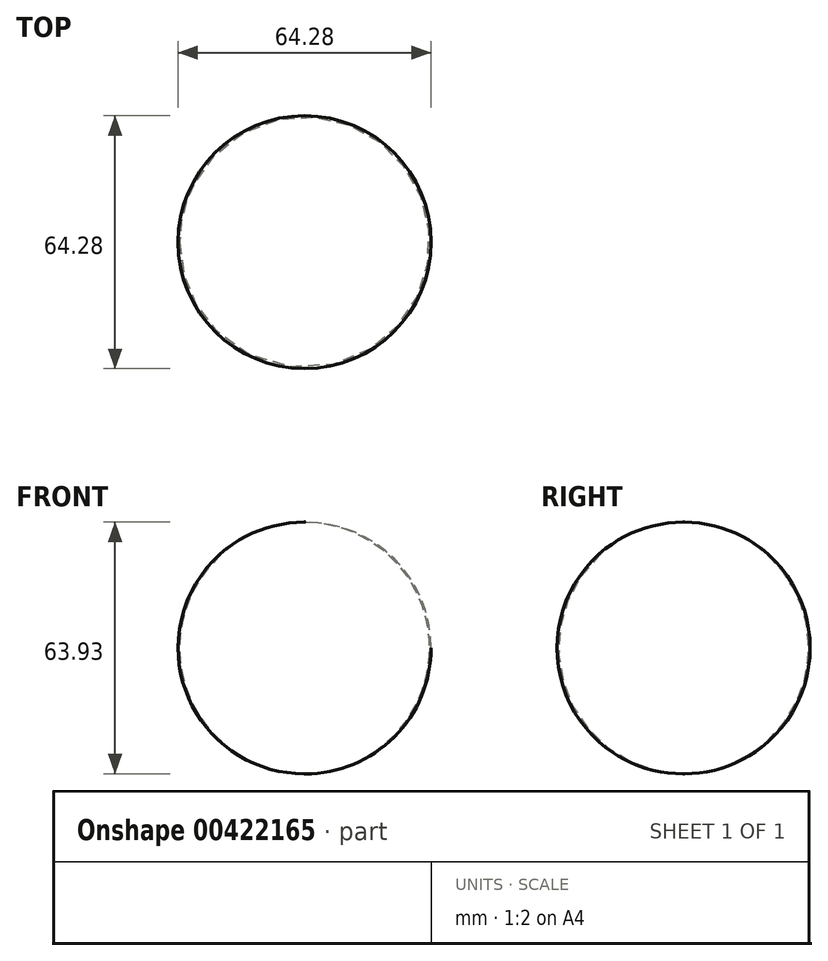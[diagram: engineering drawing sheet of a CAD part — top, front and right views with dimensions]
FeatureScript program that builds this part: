
annotation { "Feature Type Name" : "Feature", "Feature Type Description" : "" }
export const myFeature = defineFeature(function(context is Context, id is Id, definition is map)
    precondition{}
    {
        {
            var Q0;
            Q0=qCreatedBy(makeId("Front.planeOp"),FACE);
            var sketch = newSketch(context, id + "F0", { "sketchPlane" : qUnion([Q0])});
            skArc(sketch, "E0", {"start": v(0, -24.37) * mm, "mid": v(31.79, 7.6) * mm, "end": v(0, 39.56) * mm});
            skLineSegment(sketch, "E1", {"start": v(0, 39.56) * mm, "end": v(0, -24.37) * mm});
            skSolve(sketch);
        }
        {
            var Q0;
            Q0 = qSketchRegion(id + "F0", true);
            var Q1;
            Q1=sQuery(id+"F0.wireOp",EDGE,"E1");
            revolve(context, id + "F1", {"entities" : qUnion([Q0]), "axis" : qUnion([Q1]), "revolveType" : RevolveType.FULL});
        }
    });
